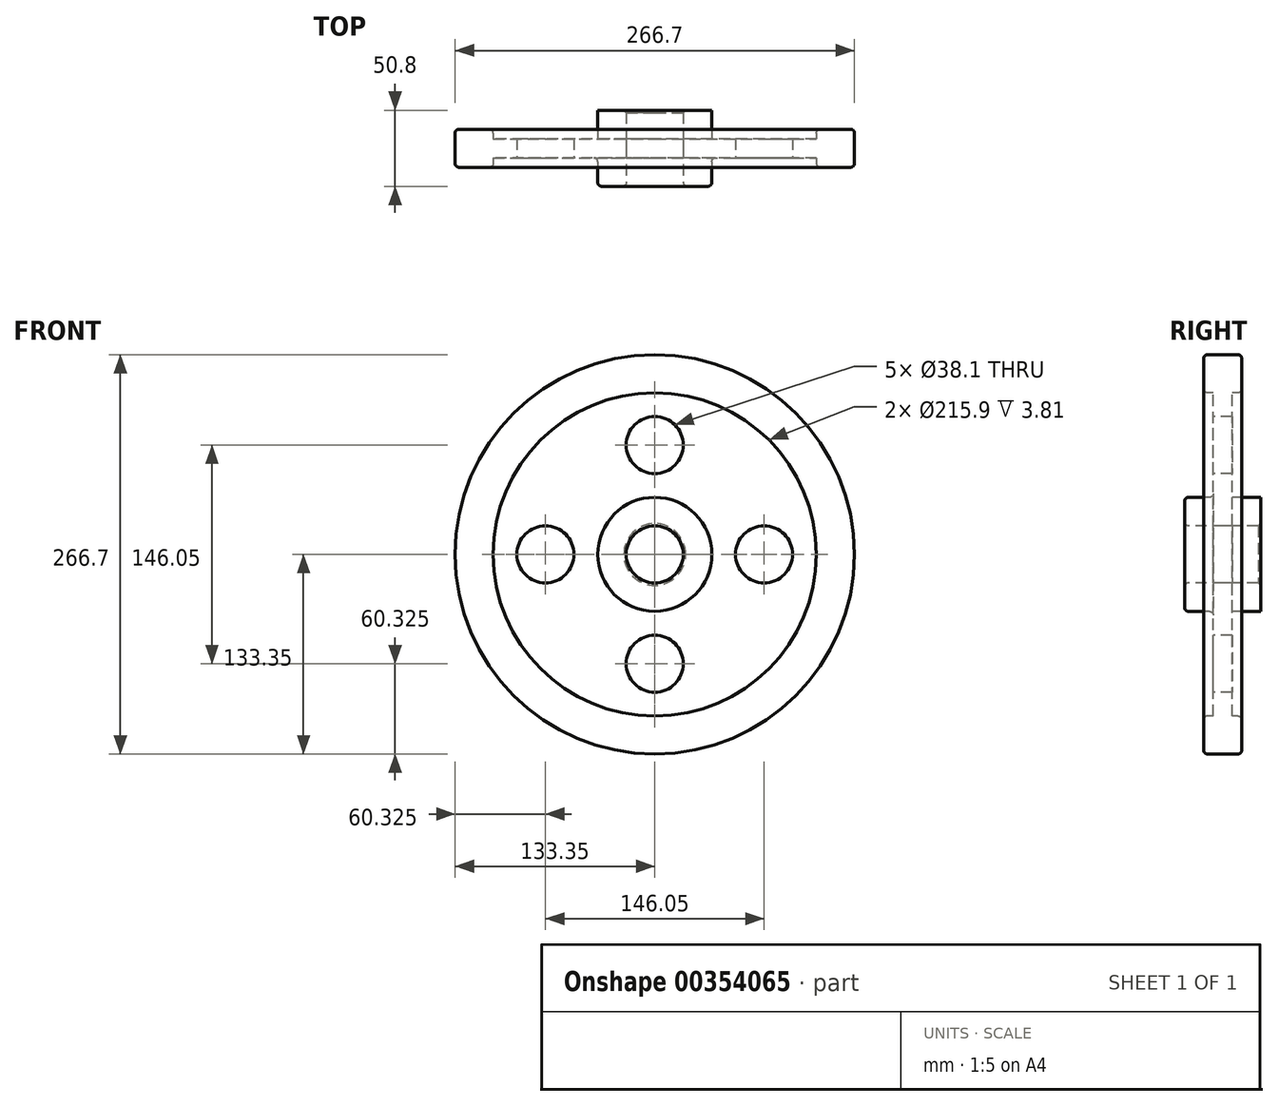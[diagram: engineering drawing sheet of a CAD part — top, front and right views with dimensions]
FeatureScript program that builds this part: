
annotation { "Feature Type Name" : "Feature", "Feature Type Description" : "" }
export const myFeature = defineFeature(function(context is Context, id is Id, definition is map)
    precondition{}
    {
        {
            var Q0;
            Q0=qCreatedBy(makeId("Right.planeOp"),FACE);
            var sketch = newSketch(context, id + "F0", { "sketchPlane" : qUnion([Q0])});
            skLineSegment(sketch, "E0", {"start": v(0, 0) * mm, "end": v(75.6, 0) * mm, "construction": true});
            skLineSegment(sketch, "E1.0", {"start": v(0, 19.05) * mm, "end": v(12.7, 19.05) * mm});
            skLineSegment(sketch, "E2.0", {"start": v(6.35, 38.1) * mm, "end": v(12.7, 38.1) * mm});
            skLineSegment(sketch, "E3.0", {"start": v(6.35, 107.95) * mm, "end": v(12.7, 107.95) * mm});
            skLineSegment(sketch, "E4.0", {"start": v(0, 133.35) * mm, "end": v(12.7, 133.35) * mm});
            skLineSegment(sketch, "E5", {"start": v(0, 133.35) * mm, "end": v(0, 0) * mm, "construction": true});
            skLineSegment(sketch, "E6.0", {"start": v(25.4, 38.1) * mm, "end": v(25.4, 19.05) * mm});
            skLineSegment(sketch, "E7.0", {"start": v(6.35, 107.95) * mm, "end": v(6.35, 38.1) * mm});
            skLineSegment(sketch, "E8.0", {"start": v(12.7, 133.35) * mm, "end": v(12.7, 107.95) * mm});
            skLineSegment(sketch, "E9", {"start": v(12.7, 38.1) * mm, "end": v(25.4, 38.1) * mm});
            skLineSegment(sketch, "E10", {"start": v(25.4, 19.05) * mm, "end": v(12.94, 19.31) * mm});
            skLineSegment(sketch, "E11.MirrorCS", {"start": v(0, 133.35) * mm, "end": v(-12.7, 133.35) * mm});
            skLineSegment(sketch, "E12.MirrorCS", {"start": v(-12.7, 133.35) * mm, "end": v(-12.7, 107.95) * mm});
            skLineSegment(sketch, "E13.MirrorCS", {"start": v(-6.35, 107.95) * mm, "end": v(-6.35, 38.1) * mm});
            skLineSegment(sketch, "E14.MirrorCS", {"start": v(-12.7, 38.1) * mm, "end": v(-25.4, 38.1) * mm});
            skLineSegment(sketch, "E15.MirrorCS", {"start": v(-25.4, 38.1) * mm, "end": v(-25.4, 19.05) * mm});
            skLineSegment(sketch, "E16.MirrorCS", {"start": v(-25.4, 19.05) * mm, "end": v(-12.94, 19.31) * mm});
            skLineSegment(sketch, "E17.MirrorCS", {"start": v(0, 19.05) * mm, "end": v(-12.7, 19.05) * mm});
            skLineSegment(sketch, "E18", {"start": v(-12.7, 107.95) * mm, "end": v(-6.35, 107.95) * mm});
            skLineSegment(sketch, "E19", {"start": v(-12.7, 38.1) * mm, "end": v(-6.35, 38.1) * mm});
            skLineSegment(sketch, "E20", {"start": v(-12.7, 133.35) * mm, "end": v(12.7, 133.35) * mm});
            skLineSegment(sketch, "E21", {"start": v(-6.35, 38.1) * mm, "end": v(-12.7, 38.1) * mm});
            skLineSegment(sketch, "E22", {"start": v(-25.4, 19.05) * mm, "end": v(25.4, 19.05) * mm});
            skLineSegment(sketch, "E23", {"start": v(25.4, 19.05) * mm, "end": v(25.4, 38.1) * mm});
            skLineSegment(sketch, "E24", {"start": v(25.4, 38.1) * mm, "end": v(12.7, 38.1) * mm});
            skLineSegment(sketch, "E25", {"start": v(12.7, 38.1) * mm, "end": v(6.35, 38.1) * mm});
            skLineSegment(sketch, "E26", {"start": v(6.35, 38.1) * mm, "end": v(6.35, 107.95) * mm});
            skSolve(sketch);
        }
        {
            var Q0;
            Q0=makeQuery(id+"F0.imprint","IMPRINT",FACE,{"disambiguationData":[TD([[makeQuery(id+"F0.imprint","IMPRINT",EDGE,{"derivedFrom":sQuery(id+"F0.wireOp",EDGE,"E3.0")}),1.0]])]});
            var Q1;
            Q1=sQuery(id+"F0.wireOp",EDGE,"E0");
            revolve(context, id + "F1", {"entities" : qUnion([Q0]), "axis" : qUnion([Q1]), "revolveType" : RevolveType.FULL});
        }
        {
            var Q0;
            Q0=makeQuery(id+"F1.opRevolve","SWEPT_FACE",FACE,{"disambiguationData":[OSD([sQuery(id+"F0.wireOp",EDGE,"E13.MirrorCS")])]});
            var sketch = newSketch(context, id + "F2", { "sketchPlane" : qUnion([Q0])});
            skPoint(sketch, "E27.start.orphan", {"position": v(0, 0) * mm});
            skLineSegment(sketch, "E28", {"start": v(0, 0) * mm, "end": v(0, 73.03) * mm});
            skCircle(sketch, "E29", {"center": v(0, 73.03) * mm, "radius": 19.05 * mm});
            skCircle(sketch, "E30.1.0", {"center": v(-73.03, 0) * mm, "radius": 19.05 * mm});
            skCircle(sketch, "E30.2.0", {"center": v(0, -73.03) * mm, "radius": 19.05 * mm});
            skCircle(sketch, "E30.3.0", {"center": v(73.03, 0) * mm, "radius": 19.05 * mm});
            skSolve(sketch);
        }
        {
            var Q0;
            Q0=makeQuery(id+"F2.imprint","IMPRINT",FACE,{"disambiguationData":[TD([[makeQuery(id+"F2.imprint","IMPRINT",EDGE,{"derivedFrom":sQuery(id+"F2.wireOp",EDGE,"E30.1.0")}),1.0]])]});
            var Q1;
            Q1=makeQuery(id+"F2.imprint","IMPRINT",FACE,{"disambiguationData":[TD([[makeQuery(id+"F2.imprint","IMPRINT",EDGE,{"derivedFrom":sQuery(id+"F2.wireOp",EDGE,"E30.2.0")}),1.0]])]});
            var Q2;
            Q2=makeQuery(id+"F2.imprint","IMPRINT",FACE,{"disambiguationData":[TD([[makeQuery(id+"F2.imprint","IMPRINT",EDGE,{"derivedFrom":sQuery(id+"F2.wireOp",EDGE,"E30.3.0")}),1.0]])]});
            var Q3;
            Q3=makeQuery(id+"F2.imprint","IMPRINT",FACE,{"disambiguationData":[TD([[makeQuery(id+"F2.imprint","IMPRINT",EDGE,{"derivedFrom":sQuery(id+"F2.wireOp",EDGE,"E29")}),1.0]])]});
            extrude(context, id + "F3", {"entities" : qUnion([Q0, Q1, Q2, Q3]), "operationType" : NewBodyOperationType.REMOVE, "oppositeDirection" : true, "depth" : 25.4 * mm});
        }
        {
            var Q0;
            Q0=makeQuery(id+"F1.opRevolve","SWEPT_FACE",FACE,{"disambiguationData":[OSD([sQuery(id+"F0.wireOp",EDGE,"E14.MirrorCS"),sQuery(id+"F0.wireOp",EDGE,"E21")])]});
            var Q1;
            Q1=makeQuery(id+"F1.opRevolve","SWEPT_EDGE",EDGE,{"disambiguationData":[OSD([sQuery(id+"F0.wireOp",EDGE,"E14.MirrorCS"),sQuery(id+"F0.wireOp",EDGE,"E15.MirrorCS")])]});
            var Q2;
            Q2=makeQuery(id+"F1.opRevolve","SWEPT_FACE",FACE,{"disambiguationData":[OSD([sQuery(id+"F0.wireOp",EDGE,"E15.MirrorCS")])]});
            var Q3;
            Q3=makeQuery(id+"F1.opRevolve","SWEPT_FACE",FACE,{"disambiguationData":[OSD([sQuery(id+"F0.wireOp",EDGE,"E24"),sQuery(id+"F0.wireOp",EDGE,"E25")])]});
            var Q4;
            Q4=makeQuery(id+"F1.opRevolve","SWEPT_EDGE",EDGE,{"disambiguationData":[OSD([sQuery(id+"F0.wireOp",EDGE,"E23"),sQuery(id+"F0.wireOp",EDGE,"E24")])]});
            var Q5;
            Q5=makeQuery(id+"F1.opRevolve","SWEPT_EDGE",EDGE,{"disambiguationData":[OSD([sQuery(id+"F0.wireOp",EDGE,"E20"),sQuery(id+"F0.wireOp",EDGE,"E12.MirrorCS")])]});
            var Q6;
            Q6=makeQuery(id+"F1.opRevolve","SWEPT_EDGE",EDGE,{"disambiguationData":[OSD([sQuery(id+"F0.wireOp",EDGE,"E8.0"),sQuery(id+"F0.wireOp",EDGE,"E20")])]});
            fillet(context, id + "F4", {"entities" : qUnion([Q0, Q1, Q2, Q3, Q4, Q5, Q6]), "radius" : 2.54 * mm, "tangentPropagation" : true, "allowEdgeOverflow" : false});
        }
        {
            var Q0;
            {var subQ0=sQuery(id+"F0.wireOp",EDGE,"E15.MirrorCS");Q0=makeQuery(id+"F4.opFillet","BLEND_EDGE",EDGE,{"blendedFrom":[makeQuery(id+"F1.opRevolve","SWEPT_EDGE",EDGE,{"disambiguationData":[OSD([subQ0,sQuery(id+"F0.wireOp",EDGE,"E22")])]}),makeQuery(id+"F1.opRevolve","SWEPT_FACE",FACE,{"disambiguationData":[OSD([subQ0])]})],"blendedInto":[makeQuery(id+"F1.opRevolve","SWEPT_FACE",FACE,{"disambiguationData":[OSD([subQ0])]})]});}
            var Q1;
            Q1=makeQuery(id+"F1.opRevolve","SWEPT_EDGE",EDGE,{"disambiguationData":[OSD([sQuery(id+"F0.wireOp",EDGE,"E22"),sQuery(id+"F0.wireOp",EDGE,"E23")])]});
            chamfer(context, id + "F5", {"entities" : qUnion([Q0, Q1]), "width" : 1.6 * mm, "tangentPropagation" : true});
        }
    });
